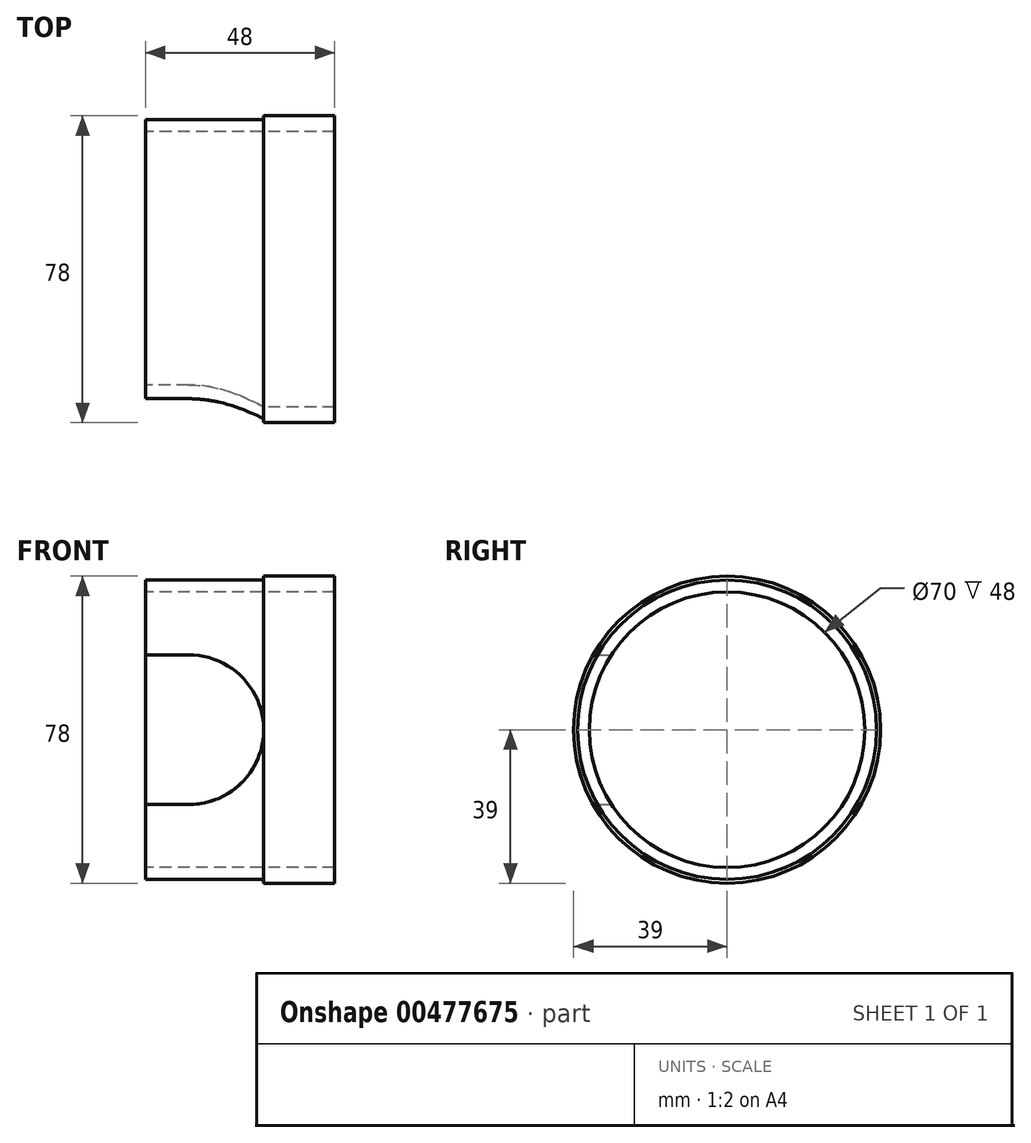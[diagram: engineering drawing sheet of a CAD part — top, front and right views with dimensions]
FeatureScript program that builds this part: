
annotation { "Feature Type Name" : "Feature", "Feature Type Description" : "" }
export const myFeature = defineFeature(function(context is Context, id is Id, definition is map)
    precondition{}
    {
        {
            var Q0;
            Q0=qCreatedBy(makeId("Front.planeOp"),FACE);
            var sketch = newSketch(context, id + "F0", { "sketchPlane" : qUnion([Q0])});
            skLineSegment(sketch, "E0", {"start": v(-160.59, 0) * mm, "end": v(160.06, 0) * mm, "construction": true});
            skLineSegment(sketch, "E1", {"start": v(-36.5, 38) * mm, "end": v(-6.5, 38) * mm});
            skLineSegment(sketch, "E2", {"start": v(-36.5, 38) * mm, "end": v(-36.5, 35) * mm});
            skLineSegment(sketch, "E3.0", {"start": v(-36.5, 35) * mm, "end": v(11.5, 35) * mm});
            skLineSegment(sketch, "E4", {"start": v(11.5, 38) * mm, "end": v(11.5, 35) * mm});
            skLineSegment(sketch, "E5", {"start": v(11.47, 39) * mm, "end": v(-6.5, 39) * mm});
            skLineSegment(sketch, "E6", {"start": v(-6.5, 39) * mm, "end": v(-6.5, 38) * mm});
            skLineSegment(sketch, "E7", {"start": v(11.47, 39) * mm, "end": v(11.5, 38) * mm});
            skSolve(sketch);
        }
        {
            var Q0;
            Q0 = qSketchRegion(id + "F0", true);
            var Q1;
            Q1=sQuery(id+"F0.wireOp",EDGE,"E0");
            revolve(context, id + "F1", {"entities" : qUnion([Q0]), "axis" : qUnion([Q1]), "revolveType" : RevolveType.FULL});
        }
        {
            var Q0;
            Q0=qCreatedBy(makeId("Front.planeOp"),FACE);
            var sketch = newSketch(context, id + "F2", { "sketchPlane" : qUnion([Q0])});
            skLineSegment(sketch, "E8", {"start": v(-6.5, 86) * mm, "end": v(-6.5, -93.51) * mm, "construction": true});
            skLineSegment(sketch, "E9", {"start": v(11.2, 0) * mm, "end": v(-94.54, 0) * mm, "construction": true});
            skLineSegment(sketch, "E10", {"start": v(-25.5, 7.75) * mm, "end": v(-25.5, -8.8) * mm, "construction": true});
            skPoint(sketch, "E11", {"position": v(-25.5, 0) * mm});
            skArc(sketch, "E12", {"start": v(-25.5, -19) * mm, "mid": v(-6.5, 0.06) * mm, "end": v(-25.62, 19) * mm});
            skLineSegment(sketch, "E13", {"start": v(-25.62, 19) * mm, "end": v(-52.53, 19) * mm});
            skLineSegment(sketch, "E14", {"start": v(-25.5, -19) * mm, "end": v(-52.53, -19) * mm});
            skLineSegment(sketch, "E15", {"start": v(-52.53, 19) * mm, "end": v(-52.53, -19) * mm});
            skSolve(sketch);
        }
        {
            var Q0;
            Q0=makeQuery(id+"F2.imprint","IMPRINT",FACE,{"disambiguationData":[TD([[makeQuery(id+"F2.imprint","IMPRINT",EDGE,{"derivedFrom":sQuery(id+"F2.wireOp",EDGE,"E12")}),1.0]])]});
            extrude(context, id + "F3", {"entities" : qUnion([Q0]), "operationType" : NewBodyOperationType.REMOVE, "depth" : 40 * mm});
        }
    });
